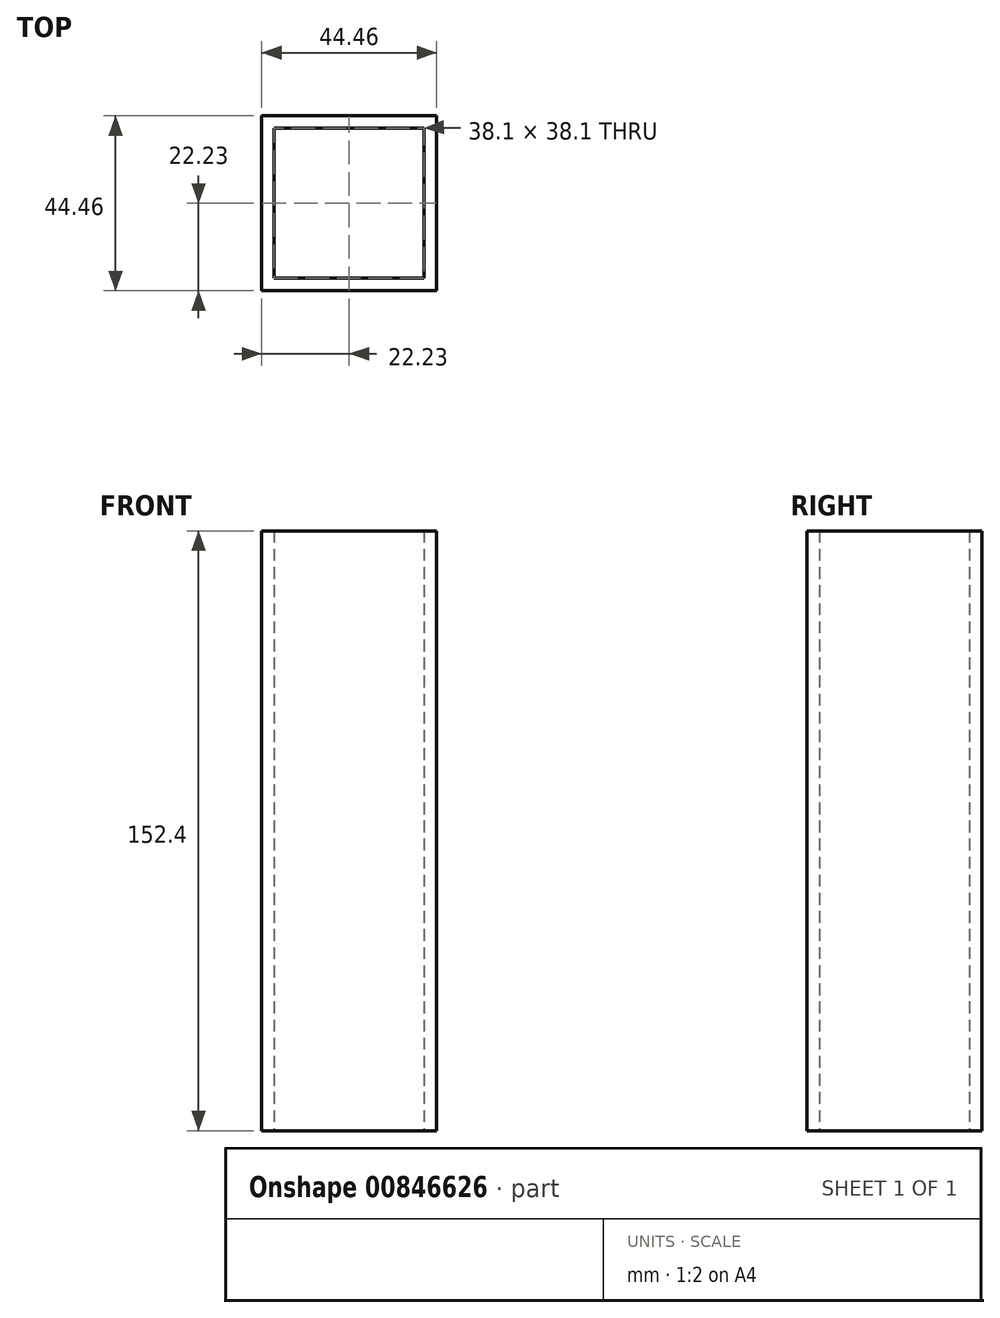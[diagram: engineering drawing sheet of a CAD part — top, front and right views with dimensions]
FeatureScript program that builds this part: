
annotation { "Feature Type Name" : "Feature", "Feature Type Description" : "" }
export const myFeature = defineFeature(function(context is Context, id is Id, definition is map)
    precondition{}
    {
        {
            var Q0;
            Q0=qCreatedBy(makeId("Top.planeOp"),FACE);
            var sketch = newSketch(context, id + "F0", { "sketchPlane" : qUnion([Q0])});
            skLineSegment(sketch, "E0.bottom", {"start": v(-19.05, 19.05) * mm, "end": v(19.05, 19.05) * mm});
            skLineSegment(sketch, "E0.top", {"start": v(-19.05, -19.05) * mm, "end": v(19.05, -19.05) * mm});
            skLineSegment(sketch, "E0.left", {"start": v(-19.05, 19.05) * mm, "end": v(-19.05, -19.05) * mm});
            skLineSegment(sketch, "E0.right", {"start": v(19.05, 19.05) * mm, "end": v(19.05, -19.05) * mm});
            skPoint(sketch, "E0.middle", {"position": v(0, 0) * mm});
            skLineSegment(sketch, "E1.bottom", {"start": v(-22.22, 22.23) * mm, "end": v(22.23, 22.23) * mm});
            skLineSegment(sketch, "E1.top", {"start": v(-22.23, -22.23) * mm, "end": v(22.22, -22.23) * mm});
            skLineSegment(sketch, "E1.left", {"start": v(-22.22, 22.23) * mm, "end": v(-22.23, -22.23) * mm});
            skLineSegment(sketch, "E1.right", {"start": v(22.23, 22.23) * mm, "end": v(22.22, -22.23) * mm});
            skSolve(sketch);
        }
        {
            var Q0;
            Q0=makeQuery(id+"F0.imprint","IMPRINT",FACE,{"disambiguationData":[TD([[makeQuery(id+"F0.imprint","IMPRINT",EDGE,{"derivedFrom":sQuery(id+"F0.wireOp",EDGE,"E0.bottom")}),1.0]])]});
            extrude(context, id + "F1", {"entities" : qUnion([Q0]), "depth" : 152.4 * mm, "offsetDistance" : 25.4 * mm});
        }
    });
